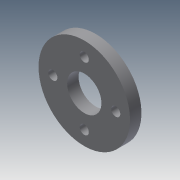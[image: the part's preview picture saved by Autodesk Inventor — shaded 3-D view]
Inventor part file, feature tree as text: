
AUTODESK INVENTOR PART (.ipt)
format: ipt  version: 2013 (Build 170138000, 138)  size: 92,160 bytes
history: native  units: mm
features: sketch x2, extrude x1
ambient origin geometry x8: Origin, YZ Plane, XZ Plane, XY Plane, X Axis, Y Axis, Z Axis, Center Point
bodies: Solid1 (feature_tree)
feature tree (3):
  extrude  "Extrusion1"  Depth=4.0mm
  sketch  "Sketch2"  dims[d9=4.0mm d10=4.0mm d11=4.0mm d12=5.0mm d13=0.0mm]
  sketch  "Sketch1"  dims[d3=15.0mm d8=4.0mm]
